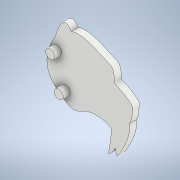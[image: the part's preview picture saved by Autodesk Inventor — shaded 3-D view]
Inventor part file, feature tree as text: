
AUTODESK INVENTOR PART (.ipt)
format: ipt  version: 2022 (Build 260153000, 153)  size: 147,456 bytes
history: native  units: in
note: dims shown in document units (in); Inventor stores cm internally (conversion verified against a paired STEP export)
features: extrude x2, sketch x1
ambient origin geometry x8: Origin, YZ Plane, XZ Plane, XY Plane, X Axis, Y Axis, Z Axis, Center Point
bodies: Solid1 (feature_tree)
feature tree (3):
  sketch  "Sketch2"  dims[d0=0.1969in d1=0.0in d2=0.1969in d3=0.0in d4=0.2559in]
  extrude  "Extrusion1"  Depth=0.1969in TaperAngle=0.0deg
  extrude  "Extrusion2"  Depth=0.2559in
